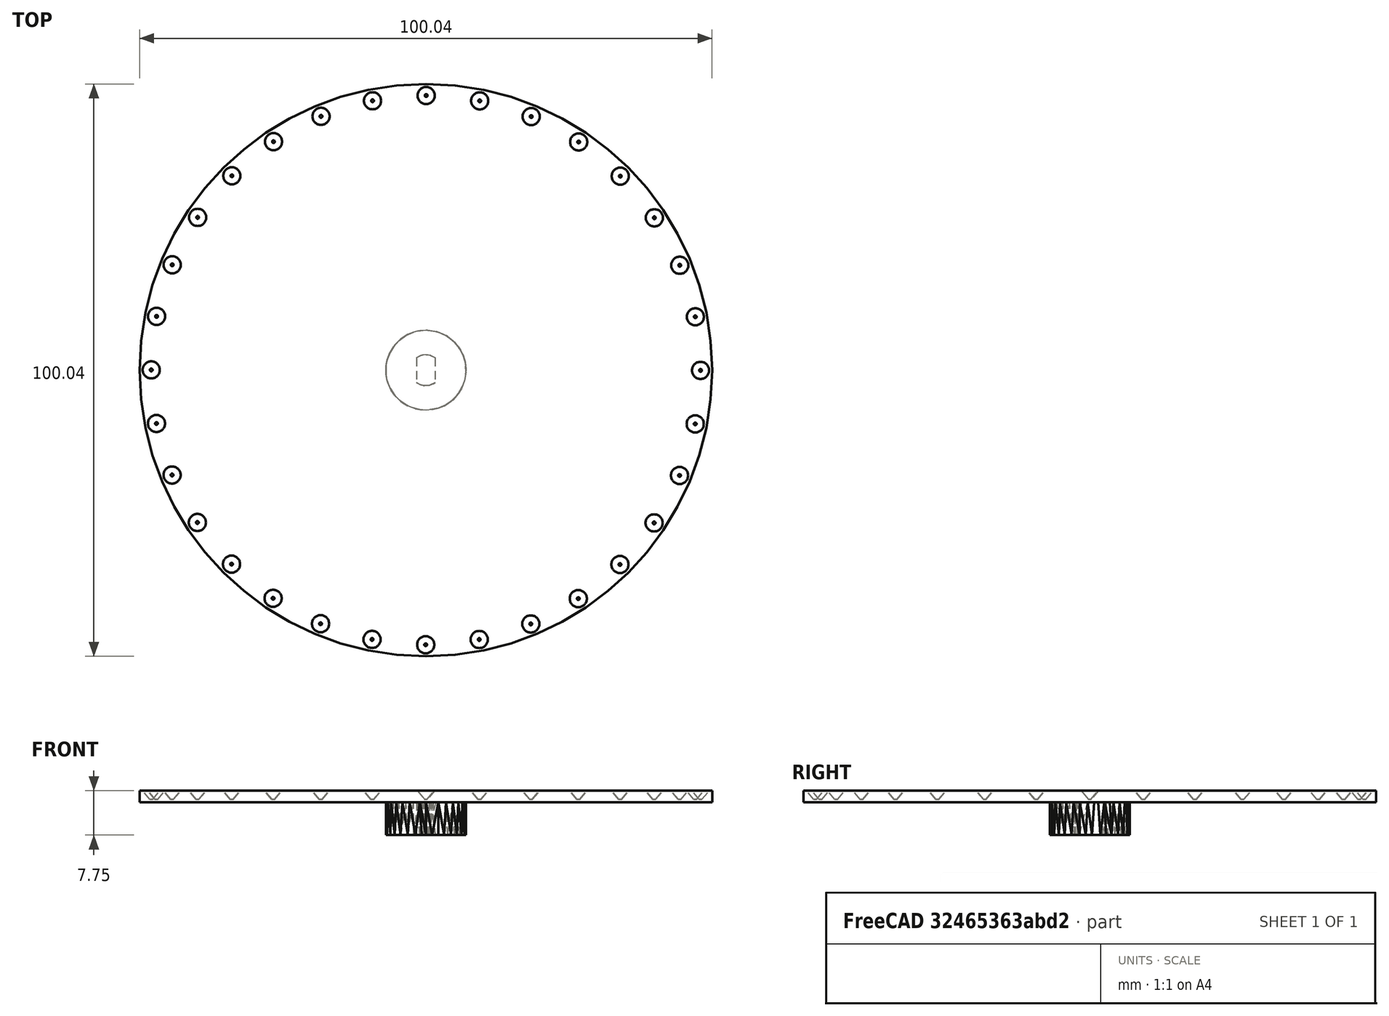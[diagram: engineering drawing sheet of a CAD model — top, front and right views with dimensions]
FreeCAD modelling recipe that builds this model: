
FCSTD DOCUMENT  (FreeCAD 0.19R24267 +148 (Git))
Label: Disc feeder
License: All rights reserved
LicenseURL: http://en.wikipedia.org/wiki/All_rights_reserved
objects: PartDesign::FeatureBase×3, PartDesign::Plane×3, Sketcher::SketchObject×3, PartDesign::Body×3, Part::Face×2, Part::FeaturePython×2, Part::Feature×1, App::DocumentObjectGroup×1, Part::Extrusion×1, PartDesign::Hole×1, PartDesign::PolarPattern×1, Part::Compound×1
note: 22 computed .brp shape members not serialized (recipe doc carries the construction recipe); baked Part::Feature solids carry a one-line shape summary decoded from their .brp

FEATURE [Part::Feature] FED_20mg_pellet_disk001_solid  label="FED_20mg_pellet_disk001 (Solid)"
  shape: bbox 43.53 x 43.54 x 8.001 mm, 3062 faces (baked)
FEATURE [PartDesign::FeatureBase] BaseFeature
  BaseFeature = -> FED_20mg_pellet_disk001_solid
FEATURE [PartDesign::Plane] DatumPlane
  Length = 119.876
  MapMode = 5
  Placement = pos=(0,0,2.25) rot=(0,0,1;0rad)
  ResizeMode = 0
  Support = -> [BaseFeature]
  Width = 119.909
FEATURE [Sketcher::SketchObject] Sketch
  FullyConstrained = false
  MapMode = 5
  Placement = pos=(0,0,2.25) rot=(0,0,1;0rad)
  Support = -> [DatumPlane]
  sketch-geometry (1):
    g0: Circle CenterX=0 CenterY=0 CenterZ=0 NormalX=0 NormalY=0 NormalZ=1 AngleXU=0 Radius=49.98
  constraints (1):
    c: Coincident(g0,g-1)
FEATURE [PartDesign::Body] Body
  BaseFeature = -> FED_20mg_pellet_disk001_solid
  Group = -> [BaseFeature,DatumPlane,Sketch]
  Origin = -> Origin
  Tip = -> BaseFeature
FEATURE [Part::Face] Face
  FaceMakerClass = Part::FaceMakerBullseye
  Sources = -> [Sketch]
FEATURE [Part::FeaturePython] Slice  # WARN: FeaturePython — macro-defined, semantics opaque (R4)
  Base = -> Body
  Mode = 1
  Tolerance = 0
  Tools = -> [Face]
FEATURE [Part::FeaturePython] Slice_child2  label="Slice.2"  # WARN: FeaturePython — macro-defined, semantics opaque (R4)
  Base = -> Slice
  FilterType = 1
  Invert = false
  OverrideMaxVal = 0
  WindowFrom = 80
  WindowTo = 100
  items = 2
FEATURE [App::DocumentObjectGroup] GrExplode_Slice  label="Exploded Slice"
  Group = -> [Slice_child2]
FEATURE [PartDesign::FeatureBase] BaseFeature001
  BaseFeature = -> Slice_child2
FEATURE [PartDesign::Plane] DatumPlane001
  Length = 60
  MapMode = 5
  Placement = pos=(0,0,8.001) rot=(0,0,1;0rad)
  ResizeMode = 0
  Support = -> [BaseFeature001]
  Width = 60
FEATURE [Sketcher::SketchObject] Sketch001
  FullyConstrained = false
  MapMode = 5
  Placement = pos=(0,0,8.001) rot=(0,0,1;0rad)
  Support = -> [DatumPlane001]
  sketch-geometry (1):
    g0: Circle CenterX=0 CenterY=0 CenterZ=0 NormalX=0 NormalY=0 NormalZ=1 AngleXU=0 Radius=50.0245
  constraints (1):
    c: Coincident(g0,g-1)
FEATURE [PartDesign::Body] Body001
  BaseFeature = -> Slice_child2
  Group = -> [BaseFeature001,DatumPlane001,Sketch001]
  Origin = -> Origin001
  Tip = -> BaseFeature001
FEATURE [Part::Face] Face001
  FaceMakerClass = Part::FaceMakerBullseye
  Sources = -> [Sketch001]
FEATURE [Part::Extrusion] Extrude
  Base = -> Sketch001
  Dir = (0,0,1)
  DirMode = 2
  FaceMakerClass = Part::FaceMakerBullseye
  LengthFwd = 2
  LengthRev = 0
  Solid = true
  Symmetric = false
FEATURE [PartDesign::FeatureBase] BaseFeature002
  BaseFeature = -> Extrude
FEATURE [PartDesign::Plane] DatumPlane002
  Length = 119.983
  MapMode = 5
  Placement = pos=(0,0,10.001) rot=(0,0,1;0rad)
  ResizeMode = 0
  Support = -> [BaseFeature002]
  Width = 120.016
FEATURE [Sketcher::SketchObject] Sketch002
  FullyConstrained = false
  MapMode = 5
  Placement = pos=(0,0,10.001) rot=(0,0,1;0rad)
  Support = -> [DatumPlane002]
  sketch-geometry (1):
    g0: Circle CenterX=0.04156 CenterY=48.0003 CenterZ=0 NormalX=0 NormalY=0 NormalZ=1 AngleXU=0 Radius=1.19738
FEATURE [PartDesign::Hole] Hole
  BaseFeature = -> BaseFeature002
  Depth = 1.5
  DepthType = 0
  Diameter = 3
  DrillForDepth = false
  DrillPoint = 0
  DrillPointAngle = 450
  HoleCutCountersinkAngle = 45
  HoleCutCustomValues = false
  HoleCutDepth = 2.7
  HoleCutDiameter = 6.1
  HoleCutType = 0
  ModelActualThread = false
  Profile = -> Sketch002
  Tapered = true
  TaperedAngle = 50
  ThreadAngle = 0
  ThreadClass = 0
  ThreadCutOffInner = 0
  ThreadCutOffOuter = 0
  ThreadDirection = 0
  ThreadFit = 0
  ThreadPitch = 0
  ThreadSize = 0
  ThreadType = 0
  Threaded = false
FEATURE [PartDesign::PolarPattern] PolarPattern
  Angle = 360
  Axis = -> Sketch002 [N_Axis]
  BaseFeature = -> Hole
  Occurrences = 32
  Originals = -> [Hole]
FEATURE [PartDesign::Body] Body002
  BaseFeature = -> Extrude
  Group = -> [BaseFeature002,DatumPlane002,Sketch002,Hole,PolarPattern]
  Origin = -> Origin002
  Tip = -> PolarPattern
FEATURE [Part::Compound] Compound
  Links = -> [Body001,Body002]
